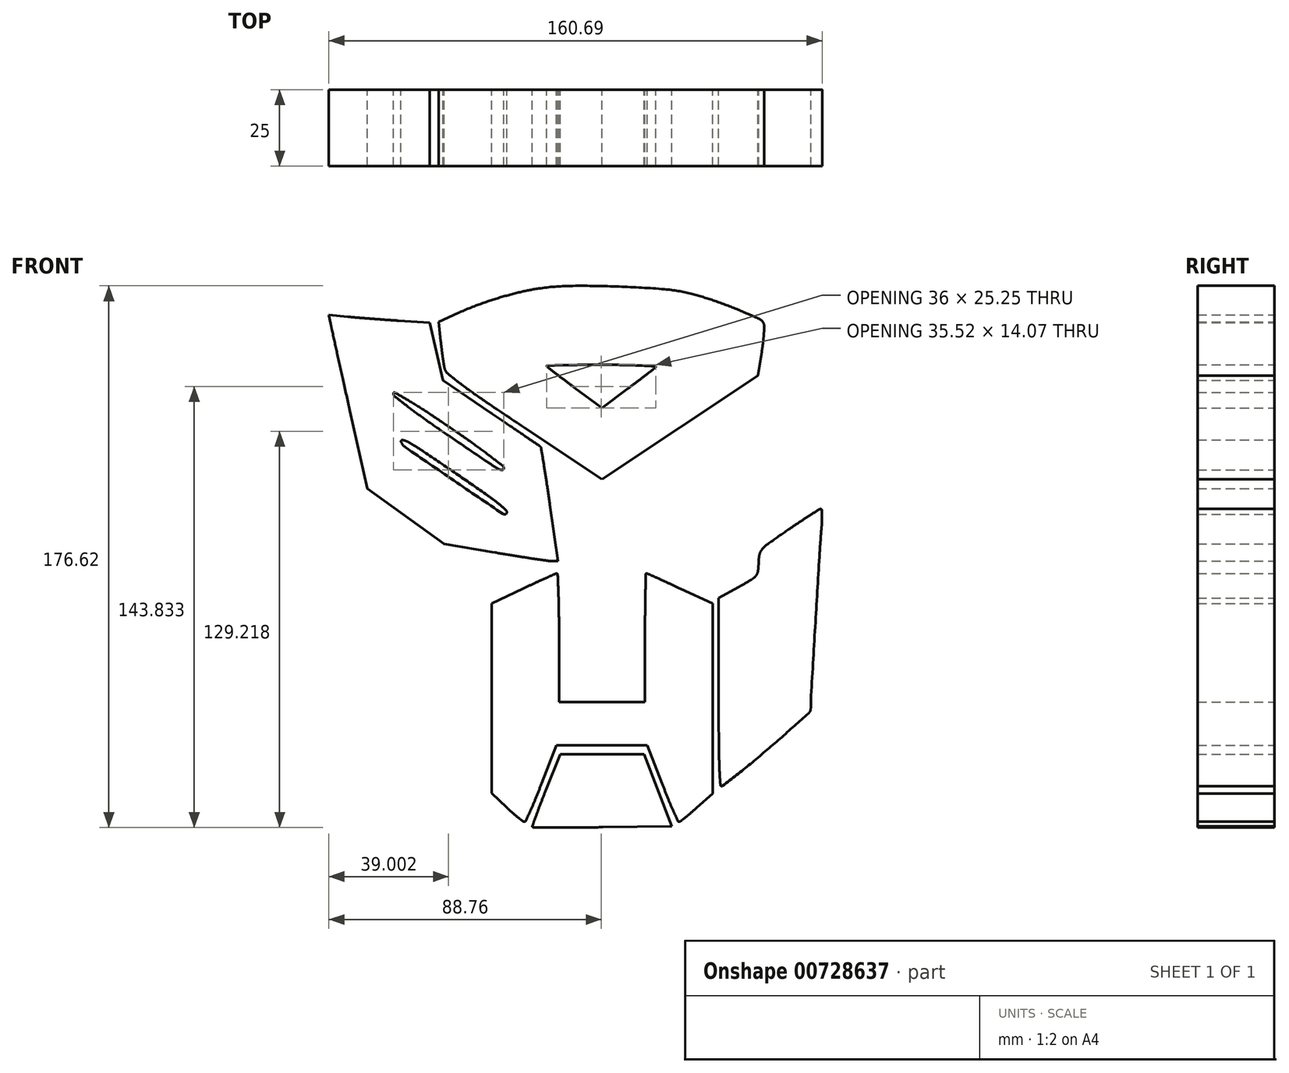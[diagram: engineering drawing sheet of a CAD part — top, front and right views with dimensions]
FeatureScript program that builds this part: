
annotation { "Feature Type Name" : "Feature", "Feature Type Description" : "" }
export const myFeature = defineFeature(function(context is Context, id is Id, definition is map)
    precondition{}
    {
        {
            var Q0;
            Q0=qCreatedBy(makeId("Front.planeOp"),FACE);
            var sketch = newSketch(context, id + "F0", { "sketchPlane" : qUnion([Q0])});
            skArc(sketch, "E0", {"start": v(-19.83, 87.54) * mm, "mid": v(-23, 87.02) * mm, "end": v(-26.16, 86.36) * mm});
            skArc(sketch, "E1", {"start": v(-26.16, 86.36) * mm, "mid": v(-29.68, 85.48) * mm, "end": v(-33.17, 84.5) * mm});
            skArc(sketch, "E2", {"start": v(-33.17, 84.5) * mm, "mid": v(-36.72, 83.37) * mm, "end": v(-40.23, 82.14) * mm});
            skArc(sketch, "E3", {"start": v(-40.23, 82.14) * mm, "mid": v(-43.53, 80.85) * mm, "end": v(-46.77, 79.46) * mm});
            skLineSegment(sketch, "E4", {"start": v(-46.77, 79.46) * mm, "end": v(-53.15, 76.56) * mm});
            skLineSegment(sketch, "E5", {"start": v(-53.15, 76.56) * mm, "end": v(-52.44, 70.3) * mm});
            skArc(sketch, "E6", {"start": v(-52.44, 70.3) * mm, "mid": v(-52.3, 69.02) * mm, "end": v(-52.13, 67.73) * mm});
            skArc(sketch, "E7", {"start": v(-52.13, 67.73) * mm, "mid": v(-51.97, 66.44) * mm, "end": v(-51.8, 65.16) * mm});
            skArc(sketch, "E8", {"start": v(-51.8, 65.16) * mm, "mid": v(-51.63, 64.04) * mm, "end": v(-51.47, 62.92) * mm});
            skArc(sketch, "E9", {"start": v(-51.47, 62.92) * mm, "mid": v(-51.36, 62.23) * mm, "end": v(-51.23, 61.56) * mm});
            skArc(sketch, "E10", {"start": v(-51.23, 61.56) * mm, "mid": v(-50.83, 60.52) * mm, "end": v(-50.11, 59.68) * mm});
            skArc(sketch, "E11", {"start": v(-50.11, 59.68) * mm, "mid": v(-47.88, 57.85) * mm, "end": v(-45.6, 56.09) * mm});
            skArc(sketch, "E12", {"start": v(-45.6, 56.09) * mm, "mid": v(-41.96, 53.43) * mm, "end": v(-38.27, 50.86) * mm});
            skArc(sketch, "E13", {"start": v(-38.27, 50.86) * mm, "mid": v(-31.8, 46.5) * mm, "end": v(-25.3, 42.15) * mm});
            skLineSegment(sketch, "E14", {"start": v(-25.3, 42.15) * mm, "end": v(0.11, 25.25) * mm});
            skLineSegment(sketch, "E15", {"start": v(0.11, 25.25) * mm, "end": v(25.52, 42.15) * mm});
            skLineSegment(sketch, "E16", {"start": v(25.52, 42.15) * mm, "end": v(50.94, 59.06) * mm});
            skLineSegment(sketch, "E17", {"start": v(50.94, 59.06) * mm, "end": v(52.14, 66.78) * mm});
            skArc(sketch, "E18", {"start": v(52.14, 66.78) * mm, "mid": v(52.37, 68.3) * mm, "end": v(52.56, 69.84) * mm});
            skArc(sketch, "E19", {"start": v(52.56, 69.84) * mm, "mid": v(52.72, 71.24) * mm, "end": v(52.84, 72.64) * mm});
            skArc(sketch, "E20", {"start": v(52.84, 72.64) * mm, "mid": v(52.91, 73.81) * mm, "end": v(52.96, 74.98) * mm});
            skArc(sketch, "E21", {"start": v(52.96, 74.98) * mm, "mid": v(52.93, 75.45) * mm, "end": v(52.81, 75.9) * mm});
            skArc(sketch, "E22", {"start": v(52.81, 75.9) * mm, "mid": v(52.21, 76.85) * mm, "end": v(51.3, 77.5) * mm});
            skArc(sketch, "E23", {"start": v(51.3, 77.5) * mm, "mid": v(47.91, 79.04) * mm, "end": v(44.5, 80.5) * mm});
            skArc(sketch, "E24", {"start": v(44.5, 80.5) * mm, "mid": v(40.67, 82.02) * mm, "end": v(36.8, 83.42) * mm});
            skArc(sketch, "E25", {"start": v(36.8, 83.42) * mm, "mid": v(33.06, 84.63) * mm, "end": v(29.29, 85.7) * mm});
            skArc(sketch, "E26", {"start": v(29.29, 85.7) * mm, "mid": v(24.9, 86.64) * mm, "end": v(20.46, 87.2) * mm});
            skArc(sketch, "E27", {"start": v(20.46, 87.2) * mm, "mid": v(13.05, 87.72) * mm, "end": v(5.63, 88.07) * mm});
            skArc(sketch, "E28", {"start": v(5.63, 88.07) * mm, "mid": v(-1.91, 88.27) * mm, "end": v(-9.45, 88.3) * mm});
            skArc(sketch, "E29", {"start": v(-9.45, 88.3) * mm, "mid": v(-14.65, 88.09) * mm, "end": v(-19.83, 87.54) * mm});
            skArc(sketch, "E30", {"start": v(17.56, 61.7) * mm, "mid": v(17.23, 61.42) * mm, "end": v(16.88, 61.15) * mm});
            skArc(sketch, "E31", {"start": v(16.88, 61.15) * mm, "mid": v(15.68, 60.22) * mm, "end": v(14.47, 59.3) * mm});
            skArc(sketch, "E32", {"start": v(14.47, 59.3) * mm, "mid": v(13.04, 58.2) * mm, "end": v(11.6, 57.1) * mm});
            skArc(sketch, "E33", {"start": v(11.6, 57.1) * mm, "mid": v(10, 55.9) * mm, "end": v(8.38, 54.68) * mm});
            skLineSegment(sketch, "E34", {"start": v(8.38, 54.68) * mm, "end": v(0.14, 48.5) * mm});
            skLineSegment(sketch, "E35", {"start": v(0.14, 48.5) * mm, "end": v(-8.87, 55.15) * mm});
            skArc(sketch, "E36", {"start": v(-8.87, 55.15) * mm, "mid": v(-10.6, 56.44) * mm, "end": v(-12.33, 57.73) * mm});
            skArc(sketch, "E37", {"start": v(-12.33, 57.73) * mm, "mid": v(-13.79, 58.84) * mm, "end": v(-15.24, 59.97) * mm});
            skArc(sketch, "E38", {"start": v(-15.24, 59.97) * mm, "mid": v(-16.5, 60.96) * mm, "end": v(-17.77, 61.95) * mm});
            skArc(sketch, "E39", {"start": v(-17.77, 61.95) * mm, "mid": v(-17.86, 62.05) * mm, "end": v(-17.89, 62.19) * mm});
            skArc(sketch, "E40", {"start": v(-17.89, 62.19) * mm, "mid": v(-17.84, 62.3) * mm, "end": v(-17.74, 62.34) * mm});
            skArc(sketch, "E41", {"start": v(-17.74, 62.34) * mm, "mid": v(-15.14, 62.4) * mm, "end": v(-12.54, 62.45) * mm});
            skArc(sketch, "E42", {"start": v(-12.54, 62.45) * mm, "mid": v(-9.6, 62.5) * mm, "end": v(-6.67, 62.53) * mm});
            skArc(sketch, "E43", {"start": v(-6.67, 62.53) * mm, "mid": v(-3.18, 62.55) * mm, "end": v(0.31, 62.56) * mm});
            skArc(sketch, "E44", {"start": v(0.31, 62.56) * mm, "mid": v(3.77, 62.54) * mm, "end": v(7.23, 62.5) * mm});
            skArc(sketch, "E45", {"start": v(7.23, 62.5) * mm, "mid": v(10.06, 62.42) * mm, "end": v(12.89, 62.3) * mm});
            skArc(sketch, "E46", {"start": v(12.89, 62.3) * mm, "mid": v(15.17, 62.19) * mm, "end": v(17.45, 62.05) * mm});
            skArc(sketch, "E47", {"start": v(17.45, 62.05) * mm, "mid": v(17.62, 61.92) * mm, "end": v(17.56, 61.7) * mm});
            skArc(sketch, "E48", {"start": v(-88.3, 75.94) * mm, "mid": v(-88.08, 74.93) * mm, "end": v(-87.87, 73.92) * mm});
            skArc(sketch, "E49", {"start": v(-87.87, 73.92) * mm, "mid": v(-87.04, 70.17) * mm, "end": v(-86.21, 66.43) * mm});
            skArc(sketch, "E50", {"start": v(-86.21, 66.43) * mm, "mid": v(-85.24, 62) * mm, "end": v(-84.25, 57.57) * mm});
            skArc(sketch, "E51", {"start": v(-84.25, 57.57) * mm, "mid": v(-83.15, 52.59) * mm, "end": v(-82.04, 47.61) * mm});
            skLineSegment(sketch, "E52", {"start": v(-82.04, 47.61) * mm, "end": v(-76.39, 22.17) * mm});
            skLineSegment(sketch, "E53", {"start": v(-76.39, 22.17) * mm, "end": v(-63.89, 13.17) * mm});
            skLineSegment(sketch, "E54", {"start": v(-63.89, 13.17) * mm, "end": v(-51.39, 4.18) * mm});
            skLineSegment(sketch, "E55", {"start": v(-51.39, 4.18) * mm, "end": v(-34.89, 1.38) * mm});
            skArc(sketch, "E56", {"start": v(-34.89, 1.38) * mm, "mid": v(-31.65, 0.84) * mm, "end": v(-28.42, 0.3) * mm});
            skArc(sketch, "E57", {"start": v(-28.42, 0.3) * mm, "mid": v(-25.52, -0.15) * mm, "end": v(-22.63, -0.6) * mm});
            skArc(sketch, "E58", {"start": v(-22.63, -0.6) * mm, "mid": v(-20.18, -0.97) * mm, "end": v(-17.74, -1.32) * mm});
            skArc(sketch, "E59", {"start": v(-17.74, -1.32) * mm, "mid": v(-17.03, -1.4) * mm, "end": v(-16.31, -1.43) * mm});
            skLineSegment(sketch, "E60", {"start": v(-16.31, -1.43) * mm, "end": v(-14.24, -1.44) * mm});
            skLineSegment(sketch, "E61", {"start": v(-14.24, -1.44) * mm, "end": v(-16.89, 17.04) * mm});
            skArc(sketch, "E62", {"start": v(-16.89, 17.04) * mm, "mid": v(-17.4, 20.6) * mm, "end": v(-17.93, 24.16) * mm});
            skArc(sketch, "E63", {"start": v(-17.93, 24.16) * mm, "mid": v(-18.4, 27.18) * mm, "end": v(-18.88, 30.2) * mm});
            skArc(sketch, "E64", {"start": v(-18.88, 30.2) * mm, "mid": v(-19.32, 32.86) * mm, "end": v(-19.76, 35.53) * mm});
            skArc(sketch, "E65", {"start": v(-19.76, 35.53) * mm, "mid": v(-19.83, 35.72) * mm, "end": v(-19.96, 35.87) * mm});
            skArc(sketch, "E66", {"start": v(-19.96, 35.87) * mm, "mid": v(-20.13, 36) * mm, "end": v(-20.3, 36.13) * mm});
            skArc(sketch, "E67", {"start": v(-20.3, 36.13) * mm, "mid": v(-22.59, 37.69) * mm, "end": v(-24.86, 39.25) * mm});
            skArc(sketch, "E68", {"start": v(-24.86, 39.25) * mm, "mid": v(-27.44, 41) * mm, "end": v(-30.02, 42.76) * mm});
            skArc(sketch, "E69", {"start": v(-30.02, 42.76) * mm, "mid": v(-33.03, 44.82) * mm, "end": v(-36.05, 46.87) * mm});
            skLineSegment(sketch, "E70", {"start": v(-36.05, 46.87) * mm, "end": v(-51.72, 57.53) * mm});
            skLineSegment(sketch, "E71", {"start": v(-51.72, 57.53) * mm, "end": v(-53.85, 66.9) * mm});
            skLineSegment(sketch, "E72", {"start": v(-53.85, 66.9) * mm, "end": v(-55.99, 76.28) * mm});
            skLineSegment(sketch, "E73", {"start": v(-55.99, 76.28) * mm, "end": v(-66.19, 76.95) * mm});
            skArc(sketch, "E74", {"start": v(-66.19, 76.95) * mm, "mid": v(-68.37, 77.1) * mm, "end": v(-70.55, 77.25) * mm});
            skArc(sketch, "E75", {"start": v(-70.55, 77.25) * mm, "mid": v(-72.89, 77.42) * mm, "end": v(-75.23, 77.6) * mm});
            skArc(sketch, "E76", {"start": v(-75.23, 77.6) * mm, "mid": v(-77.38, 77.77) * mm, "end": v(-79.54, 77.94) * mm});
            skArc(sketch, "E77", {"start": v(-79.54, 77.94) * mm, "mid": v(-81.09, 78.08) * mm, "end": v(-82.64, 78.22) * mm});
            skLineSegment(sketch, "E78", {"start": v(-82.64, 78.22) * mm, "end": v(-88.9, 78.83) * mm});
            skLineSegment(sketch, "E79", {"start": v(-88.9, 78.83) * mm, "end": v(-88.3, 75.94) * mm});
            skArc(sketch, "E80", {"start": v(-31.89, 28.83) * mm, "mid": v(-32.06, 28.43) * mm, "end": v(-32.47, 28.29) * mm});
            skArc(sketch, "E81", {"start": v(-32.47, 28.29) * mm, "mid": v(-33.17, 28.42) * mm, "end": v(-33.83, 28.71) * mm});
            skArc(sketch, "E82", {"start": v(-33.83, 28.71) * mm, "mid": v(-35.5, 29.75) * mm, "end": v(-37.15, 30.83) * mm});
            skArc(sketch, "E83", {"start": v(-37.15, 30.83) * mm, "mid": v(-44.15, 35.57) * mm, "end": v(-51.14, 40.31) * mm});
            skArc(sketch, "E84", {"start": v(-51.14, 40.31) * mm, "mid": v(-54.36, 42.53) * mm, "end": v(-57.56, 44.78) * mm});
            skArc(sketch, "E85", {"start": v(-57.56, 44.78) * mm, "mid": v(-60.28, 46.76) * mm, "end": v(-62.97, 48.79) * mm});
            skArc(sketch, "E86", {"start": v(-62.97, 48.79) * mm, "mid": v(-65.22, 50.53) * mm, "end": v(-67.46, 52.3) * mm});
            skArc(sketch, "E87", {"start": v(-67.46, 52.3) * mm, "mid": v(-67.77, 52.69) * mm, "end": v(-67.89, 53.18) * mm});
            skArc(sketch, "E88", {"start": v(-67.89, 53.18) * mm, "mid": v(-67.71, 53.48) * mm, "end": v(-67.37, 53.49) * mm});
            skArc(sketch, "E89", {"start": v(-67.37, 53.49) * mm, "mid": v(-65.2, 52.25) * mm, "end": v(-63.06, 51) * mm});
            skArc(sketch, "E90", {"start": v(-63.06, 51) * mm, "mid": v(-60.22, 49.26) * mm, "end": v(-57.4, 47.46) * mm});
            skArc(sketch, "E91", {"start": v(-57.4, 47.46) * mm, "mid": v(-53.64, 44.97) * mm, "end": v(-49.89, 42.45) * mm});
            skArc(sketch, "E92", {"start": v(-49.89, 42.45) * mm, "mid": v(-46.43, 40.07) * mm, "end": v(-42.99, 37.66) * mm});
            skArc(sketch, "E93", {"start": v(-42.99, 37.66) * mm, "mid": v(-40.06, 35.55) * mm, "end": v(-37.18, 33.4) * mm});
            skArc(sketch, "E94", {"start": v(-37.18, 33.4) * mm, "mid": v(-34.73, 31.54) * mm, "end": v(-32.3, 29.67) * mm});
            skArc(sketch, "E95", {"start": v(-32.3, 29.67) * mm, "mid": v(-32, 29.3) * mm, "end": v(-31.89, 28.83) * mm});
            skArc(sketch, "E96", {"start": v(-47.37, 27.03) * mm, "mid": v(-42.58, 23.74) * mm, "end": v(-37.8, 20.42) * mm});
            skArc(sketch, "E97", {"start": v(-37.8, 20.42) * mm, "mid": v(-35.56, 18.8) * mm, "end": v(-33.36, 17.1) * mm});
            skArc(sketch, "E98", {"start": v(-33.36, 17.1) * mm, "mid": v(-32.2, 16.1) * mm, "end": v(-31.1, 15.03) * mm});
            skArc(sketch, "E99", {"start": v(-31.1, 15.03) * mm, "mid": v(-30.9, 14.51) * mm, "end": v(-31.11, 14) * mm});
            skArc(sketch, "E100", {"start": v(-31.11, 14) * mm, "mid": v(-31.6, 13.76) * mm, "end": v(-32.14, 13.9) * mm});
            skArc(sketch, "E101", {"start": v(-32.14, 13.9) * mm, "mid": v(-40.2, 19.39) * mm, "end": v(-48.24, 24.88) * mm});
            skArc(sketch, "E102", {"start": v(-48.24, 24.88) * mm, "mid": v(-56.1, 30.27) * mm, "end": v(-63.95, 35.68) * mm});
            skArc(sketch, "E103", {"start": v(-63.95, 35.68) * mm, "mid": v(-64.78, 36.44) * mm, "end": v(-65.35, 37.42) * mm});
            skArc(sketch, "E104", {"start": v(-65.35, 37.42) * mm, "mid": v(-65.28, 37.87) * mm, "end": v(-64.84, 38.03) * mm});
            skArc(sketch, "E105", {"start": v(-64.84, 38.03) * mm, "mid": v(-63.8, 37.72) * mm, "end": v(-62.8, 37.25) * mm});
            skArc(sketch, "E106", {"start": v(-62.8, 37.25) * mm, "mid": v(-60.4, 35.8) * mm, "end": v(-58.03, 34.26) * mm});
            skArc(sketch, "E107", {"start": v(-58.03, 34.26) * mm, "mid": v(-52.7, 30.66) * mm, "end": v(-47.37, 27.03) * mm});
            skArc(sketch, "E108", {"start": v(80.61, 78.05) * mm, "mid": v(80.25, 77.94) * mm, "end": v(79.87, 77.89) * mm});
            skArc(sketch, "E109", {"start": v(79.87, 77.89) * mm, "mid": v(78.17, 77.74) * mm, "end": v(76.47, 77.6) * mm});
            skArc(sketch, "E110", {"start": v(76.47, 77.6) * mm, "mid": v(74.47, 77.45) * mm, "end": v(72.47, 77.31) * mm});
            skArc(sketch, "E111", {"start": v(72.47, 77.31) * mm, "mid": v(70.2, 77.17) * mm, "end": v(67.91, 77.03) * mm});
            skLineSegment(sketch, "E112", {"start": v(67.91, 77.03) * mm, "end": v(56.21, 76.36) * mm});
            skLineSegment(sketch, "E113", {"start": v(56.21, 76.36) * mm, "end": v(54.05, 67) * mm});
            skLineSegment(sketch, "E114", {"start": v(54.05, 67) * mm, "end": v(51.89, 57.65) * mm});
            skLineSegment(sketch, "E115", {"start": v(51.89, 57.65) * mm, "end": v(36.25, 46.94) * mm});
            skArc(sketch, "E116", {"start": v(36.25, 46.94) * mm, "mid": v(33.24, 44.88) * mm, "end": v(30.23, 42.81) * mm});
            skArc(sketch, "E117", {"start": v(30.23, 42.81) * mm, "mid": v(27.66, 41.05) * mm, "end": v(25.09, 39.28) * mm});
            skArc(sketch, "E118", {"start": v(25.09, 39.28) * mm, "mid": v(22.81, 37.72) * mm, "end": v(20.54, 36.15) * mm});
            skArc(sketch, "E119", {"start": v(20.54, 36.15) * mm, "mid": v(20.37, 36.03) * mm, "end": v(20.2, 35.9) * mm});
            skArc(sketch, "E120", {"start": v(20.2, 35.9) * mm, "mid": v(19.86, 35.5) * mm, "end": v(19.7, 35) * mm});
            skArc(sketch, "E121", {"start": v(19.7, 35) * mm, "mid": v(18.38, 26.14) * mm, "end": v(17.07, 17.28) * mm});
            skArc(sketch, "E122", {"start": v(17.07, 17.28) * mm, "mid": v(15.76, 8.38) * mm, "end": v(14.45, -0.52) * mm});
            skArc(sketch, "E123", {"start": v(14.45, -0.52) * mm, "mid": v(14.49, -0.97) * mm, "end": v(14.71, -1.35) * mm});
            skArc(sketch, "E124", {"start": v(14.71, -1.35) * mm, "mid": v(14.88, -1.46) * mm, "end": v(15.08, -1.48) * mm});
            skArc(sketch, "E125", {"start": v(15.08, -1.48) * mm, "mid": v(17.68, -1.14) * mm, "end": v(20.29, -0.8) * mm});
            skArc(sketch, "E126", {"start": v(20.29, -0.8) * mm, "mid": v(23.25, -0.4) * mm, "end": v(26.2, 0.03) * mm});
            skArc(sketch, "E127", {"start": v(26.2, 0.03) * mm, "mid": v(29.68, 0.55) * mm, "end": v(33.16, 1.1) * mm});
            skLineSegment(sketch, "E128", {"start": v(33.16, 1.1) * mm, "end": v(51.22, 3.94) * mm});
            skLineSegment(sketch, "E129", {"start": v(51.22, 3.94) * mm, "end": v(63.94, 13.16) * mm});
            skLineSegment(sketch, "E130", {"start": v(63.94, 13.16) * mm, "end": v(76.66, 22.37) * mm});
            skLineSegment(sketch, "E131", {"start": v(76.66, 22.37) * mm, "end": v(82.52, 49.22) * mm});
            skArc(sketch, "E132", {"start": v(82.52, 49.22) * mm, "mid": v(83.66, 54.4) * mm, "end": v(84.8, 59.6) * mm});
            skArc(sketch, "E133", {"start": v(84.8, 59.6) * mm, "mid": v(85.8, 64.07) * mm, "end": v(86.8, 68.54) * mm});
            skArc(sketch, "E134", {"start": v(86.8, 68.54) * mm, "mid": v(87.68, 72.43) * mm, "end": v(88.56, 76.32) * mm});
            skArc(sketch, "E135", {"start": v(88.56, 76.32) * mm, "mid": v(88.69, 76.82) * mm, "end": v(88.85, 77.3) * mm});
            skArc(sketch, "E136", {"start": v(88.85, 77.3) * mm, "mid": v(88.89, 77.59) * mm, "end": v(88.8, 77.85) * mm});
            skArc(sketch, "E137", {"start": v(88.8, 77.85) * mm, "mid": v(88.58, 78.09) * mm, "end": v(88.3, 78.24) * mm});
            skArc(sketch, "E138", {"start": v(88.3, 78.24) * mm, "mid": v(87.77, 78.38) * mm, "end": v(87.23, 78.45) * mm});
            skArc(sketch, "E139", {"start": v(87.23, 78.45) * mm, "mid": v(86.35, 78.48) * mm, "end": v(85.47, 78.48) * mm});
            skArc(sketch, "E140", {"start": v(85.47, 78.48) * mm, "mid": v(84.7, 78.45) * mm, "end": v(83.92, 78.42) * mm});
            skArc(sketch, "E141", {"start": v(83.92, 78.42) * mm, "mid": v(83.19, 78.38) * mm, "end": v(82.45, 78.32) * mm});
            skArc(sketch, "E142", {"start": v(82.45, 78.32) * mm, "mid": v(81.83, 78.26) * mm, "end": v(81.22, 78.19) * mm});
            skArc(sketch, "E143", {"start": v(81.22, 78.19) * mm, "mid": v(80.91, 78.13) * mm, "end": v(80.61, 78.05) * mm});
            skArc(sketch, "E144", {"start": v(68.11, 53.07) * mm, "mid": v(67.94, 52.34) * mm, "end": v(67.45, 51.76) * mm});
            skArc(sketch, "E145", {"start": v(67.45, 51.76) * mm, "mid": v(63.76, 49.05) * mm, "end": v(60.05, 46.37) * mm});
            skArc(sketch, "E146", {"start": v(60.05, 46.37) * mm, "mid": v(55.02, 42.8) * mm, "end": v(49.95, 39.32) * mm});
            skArc(sketch, "E147", {"start": v(49.95, 39.32) * mm, "mid": v(42.43, 34.25) * mm, "end": v(34.9, 29.2) * mm});
            skArc(sketch, "E148", {"start": v(34.9, 29.2) * mm, "mid": v(34.12, 28.7) * mm, "end": v(33.33, 28.22) * mm});
            skArc(sketch, "E149", {"start": v(33.33, 28.22) * mm, "mid": v(32.99, 28.06) * mm, "end": v(32.62, 27.97) * mm});
            skArc(sketch, "E150", {"start": v(32.62, 27.97) * mm, "mid": v(32.4, 28.02) * mm, "end": v(32.25, 28.2) * mm});
            skArc(sketch, "E151", {"start": v(32.25, 28.2) * mm, "mid": v(32.15, 28.54) * mm, "end": v(32.11, 28.9) * mm});
            skArc(sketch, "E152", {"start": v(32.11, 28.9) * mm, "mid": v(32.23, 29.42) * mm, "end": v(32.57, 29.84) * mm});
            skArc(sketch, "E153", {"start": v(32.57, 29.84) * mm, "mid": v(34.88, 31.65) * mm, "end": v(37.2, 33.44) * mm});
            skArc(sketch, "E154", {"start": v(37.2, 33.44) * mm, "mid": v(40.04, 35.56) * mm, "end": v(42.9, 37.62) * mm});
            skArc(sketch, "E155", {"start": v(42.9, 37.62) * mm, "mid": v(46.37, 40.05) * mm, "end": v(49.86, 42.44) * mm});
            skArc(sketch, "E156", {"start": v(49.86, 42.44) * mm, "mid": v(53.27, 44.74) * mm, "end": v(56.69, 47.05) * mm});
            skArc(sketch, "E157", {"start": v(56.69, 47.05) * mm, "mid": v(59.58, 49) * mm, "end": v(62.47, 50.94) * mm});
            skArc(sketch, "E158", {"start": v(62.47, 50.94) * mm, "mid": v(65.07, 52.68) * mm, "end": v(67.67, 54.42) * mm});
            skArc(sketch, "E159", {"start": v(67.67, 54.42) * mm, "mid": v(67.76, 54.47) * mm, "end": v(67.86, 54.5) * mm});
            skArc(sketch, "E160", {"start": v(67.86, 54.5) * mm, "mid": v(67.92, 54.5) * mm, "end": v(67.96, 54.44) * mm});
            skArc(sketch, "E161", {"start": v(67.96, 54.44) * mm, "mid": v(68, 54.27) * mm, "end": v(68.04, 54.1) * mm});
            skArc(sketch, "E162", {"start": v(68.04, 54.1) * mm, "mid": v(68.07, 53.87) * mm, "end": v(68.1, 53.64) * mm});
            skArc(sketch, "E163", {"start": v(68.1, 53.64) * mm, "mid": v(68.1, 53.35) * mm, "end": v(68.11, 53.07) * mm});
            skArc(sketch, "E164", {"start": v(65.52, 37.3) * mm, "mid": v(64.78, 36.07) * mm, "end": v(63.72, 35.1) * mm});
            skArc(sketch, "E165", {"start": v(63.72, 35.1) * mm, "mid": v(55.98, 29.92) * mm, "end": v(48.22, 24.77) * mm});
            skArc(sketch, "E166", {"start": v(48.22, 24.77) * mm, "mid": v(40.26, 19.5) * mm, "end": v(32.28, 14.26) * mm});
            skArc(sketch, "E167", {"start": v(32.28, 14.26) * mm, "mid": v(31.68, 14.19) * mm, "end": v(31.26, 14.61) * mm});
            skArc(sketch, "E168", {"start": v(31.26, 14.61) * mm, "mid": v(31.2, 14.83) * mm, "end": v(31.15, 15.04) * mm});
            skArc(sketch, "E169", {"start": v(31.15, 15.04) * mm, "mid": v(31.12, 15.25) * mm, "end": v(31.11, 15.45) * mm});
            skArc(sketch, "E170", {"start": v(31.11, 15.45) * mm, "mid": v(31.12, 15.62) * mm, "end": v(31.15, 15.8) * mm});
            skArc(sketch, "E171", {"start": v(31.15, 15.8) * mm, "mid": v(31.19, 15.9) * mm, "end": v(31.26, 15.98) * mm});
            skArc(sketch, "E172", {"start": v(31.26, 15.98) * mm, "mid": v(32.78, 17.19) * mm, "end": v(34.36, 18.3) * mm});
            skArc(sketch, "E173", {"start": v(34.36, 18.3) * mm, "mid": v(41.62, 23.15) * mm, "end": v(48.87, 27.98) * mm});
            skArc(sketch, "E174", {"start": v(48.87, 27.98) * mm, "mid": v(56.66, 33.15) * mm, "end": v(64.44, 38.31) * mm});
            skArc(sketch, "E175", {"start": v(64.44, 38.31) * mm, "mid": v(64.83, 38.5) * mm, "end": v(65.24, 38.56) * mm});
            skArc(sketch, "E176", {"start": v(65.24, 38.56) * mm, "mid": v(65.38, 38.53) * mm, "end": v(65.5, 38.45) * mm});
            skArc(sketch, "E177", {"start": v(65.5, 38.45) * mm, "mid": v(65.6, 38.33) * mm, "end": v(65.66, 38.19) * mm});
            skArc(sketch, "E178", {"start": v(65.66, 38.19) * mm, "mid": v(65.68, 37.99) * mm, "end": v(65.67, 37.78) * mm});
            skArc(sketch, "E179", {"start": v(65.67, 37.78) * mm, "mid": v(65.6, 37.54) * mm, "end": v(65.52, 37.3) * mm});
            skArc(sketch, "E180", {"start": v(-17.43, 31.36) * mm, "mid": v(-17.26, 30.58) * mm, "end": v(-17.12, 29.8) * mm});
            skArc(sketch, "E181", {"start": v(-17.12, 29.8) * mm, "mid": v(-16.72, 27.4) * mm, "end": v(-16.32, 25) * mm});
            skArc(sketch, "E182", {"start": v(-16.32, 25) * mm, "mid": v(-15.85, 22.13) * mm, "end": v(-15.4, 19.27) * mm});
            skArc(sketch, "E183", {"start": v(-15.4, 19.27) * mm, "mid": v(-14.9, 16.1) * mm, "end": v(-14.4, 12.93) * mm});
            skArc(sketch, "E184", {"start": v(-14.4, 12.93) * mm, "mid": v(-13.7, 8.27) * mm, "end": v(-13.1, 3.6) * mm});
            skArc(sketch, "E185", {"start": v(-13.1, 3.6) * mm, "mid": v(-12.67, -0.27) * mm, "end": v(-12.36, -4.14) * mm});
            skArc(sketch, "E186", {"start": v(-12.36, -4.14) * mm, "mid": v(-12.13, -8.35) * mm, "end": v(-12, -12.57) * mm});
            skArc(sketch, "E187", {"start": v(-12, -12.57) * mm, "mid": v(-11.91, -18.45) * mm, "end": v(-11.89, -24.32) * mm});
            skLineSegment(sketch, "E188", {"start": v(-11.89, -24.32) * mm, "end": v(-11.89, -45.44) * mm});
            skLineSegment(sketch, "E189", {"start": v(-11.89, -45.44) * mm, "end": v(0.11, -45.44) * mm});
            skLineSegment(sketch, "E190", {"start": v(0.11, -45.44) * mm, "end": v(12.11, -45.44) * mm});
            skLineSegment(sketch, "E191", {"start": v(12.11, -45.44) * mm, "end": v(12.11, -23.9) * mm});
            skArc(sketch, "E192", {"start": v(12.11, -23.9) * mm, "mid": v(12.14, -17.85) * mm, "end": v(12.22, -11.8) * mm});
            skArc(sketch, "E193", {"start": v(12.22, -11.8) * mm, "mid": v(12.34, -7.63) * mm, "end": v(12.57, -3.45) * mm});
            skArc(sketch, "E194", {"start": v(12.57, -3.45) * mm, "mid": v(12.88, 0.32) * mm, "end": v(13.3, 4.08) * mm});
            skArc(sketch, "E195", {"start": v(13.3, 4.08) * mm, "mid": v(13.92, 8.62) * mm, "end": v(14.61, 13.15) * mm});
            skArc(sketch, "E196", {"start": v(14.61, 13.15) * mm, "mid": v(15.87, 21.03) * mm, "end": v(17.1, 28.91) * mm});
            skArc(sketch, "E197", {"start": v(17.1, 28.91) * mm, "mid": v(17.12, 30.26) * mm, "end": v(16.78, 31.56) * mm});
            skArc(sketch, "E198", {"start": v(16.78, 31.56) * mm, "mid": v(16.13, 32.17) * mm, "end": v(15.24, 32.08) * mm});
            skArc(sketch, "E199", {"start": v(15.24, 32.08) * mm, "mid": v(11.9, 30.04) * mm, "end": v(8.61, 27.91) * mm});
            skLineSegment(sketch, "E200", {"start": v(8.61, 27.91) * mm, "end": v(0.12, 22.26) * mm});
            skLineSegment(sketch, "E201", {"start": v(0.12, 22.26) * mm, "end": v(-6.64, 26.74) * mm});
            skArc(sketch, "E202", {"start": v(-6.64, 26.74) * mm, "mid": v(-8, 27.65) * mm, "end": v(-9.39, 28.55) * mm});
            skArc(sketch, "E203", {"start": v(-9.39, 28.55) * mm, "mid": v(-10.73, 29.41) * mm, "end": v(-12.07, 30.27) * mm});
            skArc(sketch, "E204", {"start": v(-12.07, 30.27) * mm, "mid": v(-13.23, 31) * mm, "end": v(-14.39, 31.7) * mm});
            skArc(sketch, "E205", {"start": v(-14.39, 31.7) * mm, "mid": v(-15.02, 32.09) * mm, "end": v(-15.67, 32.44) * mm});
            skArc(sketch, "E206", {"start": v(-15.67, 32.44) * mm, "mid": v(-16.36, 32.8) * mm, "end": v(-17.07, 33.14) * mm});
            skArc(sketch, "E207", {"start": v(-17.07, 33.14) * mm, "mid": v(-17.3, 33.19) * mm, "end": v(-17.52, 33.12) * mm});
            skArc(sketch, "E208", {"start": v(-17.52, 33.12) * mm, "mid": v(-17.67, 32.95) * mm, "end": v(-17.7, 32.74) * mm});
            skArc(sketch, "E209", {"start": v(-17.7, 32.74) * mm, "mid": v(-17.57, 32.04) * mm, "end": v(-17.43, 31.36) * mm});
            skArc(sketch, "E210", {"start": v(-71.4, 8.3) * mm, "mid": v(-71.11, 4.35) * mm, "end": v(-70.86, 0.38) * mm});
            skArc(sketch, "E211", {"start": v(-70.86, 0.38) * mm, "mid": v(-70.15, -11.2) * mm, "end": v(-69.46, -22.8) * mm});
            skArc(sketch, "E212", {"start": v(-69.46, -22.8) * mm, "mid": v(-68.71, -35.24) * mm, "end": v(-67.97, -47.69) * mm});
            skArc(sketch, "E213", {"start": v(-67.97, -47.69) * mm, "mid": v(-67.9, -49.08) * mm, "end": v(-67.89, -50.48) * mm});
            skArc(sketch, "E214", {"start": v(-67.89, -50.48) * mm, "mid": v(-67.78, -50.95) * mm, "end": v(-67.49, -51.34) * mm});
            skArc(sketch, "E215", {"start": v(-67.49, -51.34) * mm, "mid": v(-61.08, -56.77) * mm, "end": v(-54.68, -62.2) * mm});
            skArc(sketch, "E216", {"start": v(-54.68, -62.2) * mm, "mid": v(-48.77, -67.18) * mm, "end": v(-42.84, -72.14) * mm});
            skArc(sketch, "E217", {"start": v(-42.84, -72.14) * mm, "mid": v(-41.04, -73.54) * mm, "end": v(-39.14, -74.8) * mm});
            skArc(sketch, "E218", {"start": v(-39.14, -74.8) * mm, "mid": v(-38.7, -74.81) * mm, "end": v(-38.45, -74.45) * mm});
            skArc(sketch, "E219", {"start": v(-38.45, -74.45) * mm, "mid": v(-38.28, -71.78) * mm, "end": v(-38.14, -69.12) * mm});
            skArc(sketch, "E220", {"start": v(-38.14, -69.12) * mm, "mid": v(-38, -64.84) * mm, "end": v(-37.94, -60.56) * mm});
            skArc(sketch, "E221", {"start": v(-37.94, -60.56) * mm, "mid": v(-37.9, -52.58) * mm, "end": v(-37.89, -44.59) * mm});
            skLineSegment(sketch, "E222", {"start": v(-37.89, -44.59) * mm, "end": v(-37.89, -13.62) * mm});
            skLineSegment(sketch, "E223", {"start": v(-37.89, -13.62) * mm, "end": v(-44.39, -9.98) * mm});
            skArc(sketch, "E224", {"start": v(-44.39, -9.98) * mm, "mid": v(-46.48, -8.8) * mm, "end": v(-48.54, -7.56) * mm});
            skArc(sketch, "E225", {"start": v(-48.54, -7.56) * mm, "mid": v(-49.35, -6.98) * mm, "end": v(-50.05, -6.26) * mm});
            skArc(sketch, "E226", {"start": v(-50.05, -6.26) * mm, "mid": v(-50.48, -5.56) * mm, "end": v(-50.7, -4.76) * mm});
            skArc(sketch, "E227", {"start": v(-50.7, -4.76) * mm, "mid": v(-50.84, -3.4) * mm, "end": v(-50.89, -2.05) * mm});
            skLineSegment(sketch, "E228", {"start": v(-50.89, -2.05) * mm, "end": v(-50.89, 2.25) * mm});
            skLineSegment(sketch, "E229", {"start": v(-50.89, 2.25) * mm, "end": v(-60.88, 8.9) * mm});
            skArc(sketch, "E230", {"start": v(-60.88, 8.9) * mm, "mid": v(-62.81, 10.18) * mm, "end": v(-64.75, 11.45) * mm});
            skArc(sketch, "E231", {"start": v(-64.75, 11.45) * mm, "mid": v(-66.42, 12.53) * mm, "end": v(-68.1, 13.6) * mm});
            skArc(sketch, "E232", {"start": v(-68.1, 13.6) * mm, "mid": v(-69.56, 14.52) * mm, "end": v(-71.03, 15.44) * mm});
            skArc(sketch, "E233", {"start": v(-71.03, 15.44) * mm, "mid": v(-71.22, 15.53) * mm, "end": v(-71.42, 15.56) * mm});
            skArc(sketch, "E234", {"start": v(-71.42, 15.56) * mm, "mid": v(-71.56, 15.5) * mm, "end": v(-71.63, 15.35) * mm});
            skArc(sketch, "E235", {"start": v(-71.63, 15.35) * mm, "mid": v(-71.64, 14.4) * mm, "end": v(-71.64, 13.43) * mm});
            skArc(sketch, "E236", {"start": v(-71.64, 13.43) * mm, "mid": v(-71.63, 12.26) * mm, "end": v(-71.58, 11.09) * mm});
            skArc(sketch, "E237", {"start": v(-71.58, 11.09) * mm, "mid": v(-71.5, 9.7) * mm, "end": v(-71.4, 8.3) * mm});
            skArc(sketch, "E238", {"start": v(60.86, 8.85) * mm, "mid": v(57.67, 6.64) * mm, "end": v(54.49, 4.4) * mm});
            skArc(sketch, "E239", {"start": v(54.49, 4.4) * mm, "mid": v(53.36, 3.5) * mm, "end": v(52.34, 2.47) * mm});
            skArc(sketch, "E240", {"start": v(52.34, 2.47) * mm, "mid": v(51.76, 1.63) * mm, "end": v(51.41, 0.66) * mm});
            skArc(sketch, "E241", {"start": v(51.41, 0.66) * mm, "mid": v(51.19, -0.69) * mm, "end": v(51.11, -2.06) * mm});
            skArc(sketch, "E242", {"start": v(51.11, -2.06) * mm, "mid": v(51.06, -3.38) * mm, "end": v(50.92, -4.7) * mm});
            skArc(sketch, "E243", {"start": v(50.92, -4.7) * mm, "mid": v(50.7, -5.5) * mm, "end": v(50.26, -6.2) * mm});
            skArc(sketch, "E244", {"start": v(50.26, -6.2) * mm, "mid": v(49.56, -6.91) * mm, "end": v(48.75, -7.5) * mm});
            skArc(sketch, "E245", {"start": v(48.75, -7.5) * mm, "mid": v(46.69, -8.72) * mm, "end": v(44.61, -9.9) * mm});
            skLineSegment(sketch, "E246", {"start": v(44.61, -9.9) * mm, "end": v(38.11, -13.54) * mm});
            skLineSegment(sketch, "E247", {"start": v(38.11, -13.54) * mm, "end": v(38.11, -44.62) * mm});
            skArc(sketch, "E248", {"start": v(38.11, -44.62) * mm, "mid": v(38.12, -52.66) * mm, "end": v(38.16, -60.7) * mm});
            skArc(sketch, "E249", {"start": v(38.16, -60.7) * mm, "mid": v(38.23, -64.96) * mm, "end": v(38.36, -69.22) * mm});
            skArc(sketch, "E250", {"start": v(38.36, -69.22) * mm, "mid": v(38.5, -71.83) * mm, "end": v(38.68, -74.44) * mm});
            skArc(sketch, "E251", {"start": v(38.68, -74.44) * mm, "mid": v(38.93, -74.8) * mm, "end": v(39.36, -74.74) * mm});
            skArc(sketch, "E252", {"start": v(39.36, -74.74) * mm, "mid": v(43.95, -71.19) * mm, "end": v(48.47, -67.54) * mm});
            skArc(sketch, "E253", {"start": v(48.47, -67.54) * mm, "mid": v(53.34, -63.45) * mm, "end": v(58.15, -59.29) * mm});
            skArc(sketch, "E254", {"start": v(58.15, -59.29) * mm, "mid": v(62.78, -55.2) * mm, "end": v(67.39, -51.09) * mm});
            skArc(sketch, "E255", {"start": v(67.39, -51.09) * mm, "mid": v(67.92, -50.35) * mm, "end": v(68.11, -49.46) * mm});
            skArc(sketch, "E256", {"start": v(68.11, -49.46) * mm, "mid": v(68.14, -47.35) * mm, "end": v(68.24, -45.24) * mm});
            skArc(sketch, "E257", {"start": v(68.24, -45.24) * mm, "mid": v(68.94, -33.3) * mm, "end": v(69.65, -21.37) * mm});
            skArc(sketch, "E258", {"start": v(69.65, -21.37) * mm, "mid": v(70.33, -9.99) * mm, "end": v(71.03, 1.39) * mm});
            skArc(sketch, "E259", {"start": v(71.03, 1.39) * mm, "mid": v(71.3, 5.35) * mm, "end": v(71.62, 9.3) * mm});
            skArc(sketch, "E260", {"start": v(71.62, 9.3) * mm, "mid": v(71.7, 10.5) * mm, "end": v(71.77, 11.7) * mm});
            skArc(sketch, "E261", {"start": v(71.77, 11.7) * mm, "mid": v(71.8, 12.7) * mm, "end": v(71.78, 13.72) * mm});
            skArc(sketch, "E262", {"start": v(71.78, 13.72) * mm, "mid": v(71.74, 14.5) * mm, "end": v(71.68, 15.3) * mm});
            skArc(sketch, "E263", {"start": v(71.68, 15.3) * mm, "mid": v(71.58, 15.48) * mm, "end": v(71.4, 15.55) * mm});
            skArc(sketch, "E264", {"start": v(71.4, 15.55) * mm, "mid": v(71.11, 15.5) * mm, "end": v(70.85, 15.4) * mm});
            skArc(sketch, "E265", {"start": v(70.85, 15.4) * mm, "mid": v(69.41, 14.49) * mm, "end": v(67.98, 13.58) * mm});
            skArc(sketch, "E266", {"start": v(67.98, 13.58) * mm, "mid": v(66.31, 12.5) * mm, "end": v(64.66, 11.42) * mm});
            skArc(sketch, "E267", {"start": v(64.66, 11.42) * mm, "mid": v(62.75, 10.14) * mm, "end": v(60.86, 8.85) * mm});
            skLineSegment(sketch, "E268", {"start": v(-25.64, -10.42) * mm, "end": v(-35.89, -15.3) * mm});
            skLineSegment(sketch, "E269", {"start": v(-35.89, -15.3) * mm, "end": v(-35.89, -46.24) * mm});
            skLineSegment(sketch, "E270", {"start": v(-35.89, -46.24) * mm, "end": v(-35.89, -77.17) * mm});
            skLineSegment(sketch, "E271", {"start": v(-35.89, -77.17) * mm, "end": v(-30.93, -81.8) * mm});
            skArc(sketch, "E272", {"start": v(-30.93, -81.8) * mm, "mid": v(-29.96, -82.7) * mm, "end": v(-28.97, -83.58) * mm});
            skArc(sketch, "E273", {"start": v(-28.97, -83.58) * mm, "mid": v(-28.1, -84.34) * mm, "end": v(-27.2, -85.08) * mm});
            skArc(sketch, "E274", {"start": v(-27.2, -85.08) * mm, "mid": v(-26.44, -85.68) * mm, "end": v(-25.67, -86.28) * mm});
            skArc(sketch, "E275", {"start": v(-25.67, -86.28) * mm, "mid": v(-25.44, -86.4) * mm, "end": v(-25.18, -86.44) * mm});
            skArc(sketch, "E276", {"start": v(-25.18, -86.44) * mm, "mid": v(-24.92, -86.37) * mm, "end": v(-24.75, -86.17) * mm});
            skArc(sketch, "E277", {"start": v(-24.75, -86.17) * mm, "mid": v(-23.97, -84.47) * mm, "end": v(-23.2, -82.77) * mm});
            skArc(sketch, "E278", {"start": v(-23.2, -82.77) * mm, "mid": v(-22.32, -80.76) * mm, "end": v(-21.47, -78.74) * mm});
            skArc(sketch, "E279", {"start": v(-21.47, -78.74) * mm, "mid": v(-20.5, -76.35) * mm, "end": v(-19.57, -73.94) * mm});
            skLineSegment(sketch, "E280", {"start": v(-19.57, -73.94) * mm, "end": v(-14.75, -61.44) * mm});
            skLineSegment(sketch, "E281", {"start": v(-14.75, -61.44) * mm, "end": v(0.05, -61.44) * mm});
            skLineSegment(sketch, "E282", {"start": v(0.05, -61.44) * mm, "end": v(14.85, -61.44) * mm});
            skLineSegment(sketch, "E283", {"start": v(14.85, -61.44) * mm, "end": v(19.67, -73.94) * mm});
            skArc(sketch, "E284", {"start": v(19.67, -73.94) * mm, "mid": v(20.61, -76.34) * mm, "end": v(21.57, -78.74) * mm});
            skArc(sketch, "E285", {"start": v(21.57, -78.74) * mm, "mid": v(22.41, -80.76) * mm, "end": v(23.28, -82.77) * mm});
            skArc(sketch, "E286", {"start": v(23.28, -82.77) * mm, "mid": v(24.05, -84.49) * mm, "end": v(24.82, -86.2) * mm});
            skArc(sketch, "E287", {"start": v(24.82, -86.2) * mm, "mid": v(24.97, -86.38) * mm, "end": v(25.2, -86.44) * mm});
            skArc(sketch, "E288", {"start": v(25.2, -86.44) * mm, "mid": v(25.43, -86.4) * mm, "end": v(25.64, -86.3) * mm});
            skArc(sketch, "E289", {"start": v(25.64, -86.3) * mm, "mid": v(26.42, -85.7) * mm, "end": v(27.2, -85.1) * mm});
            skArc(sketch, "E290", {"start": v(27.2, -85.1) * mm, "mid": v(28.1, -84.36) * mm, "end": v(29, -83.61) * mm});
            skArc(sketch, "E291", {"start": v(29, -83.61) * mm, "mid": v(30, -82.74) * mm, "end": v(31, -81.85) * mm});
            skLineSegment(sketch, "E292", {"start": v(31, -81.85) * mm, "end": v(36.11, -77.26) * mm});
            skLineSegment(sketch, "E293", {"start": v(36.11, -77.26) * mm, "end": v(36.11, -46.29) * mm});
            skLineSegment(sketch, "E294", {"start": v(36.11, -46.29) * mm, "end": v(36.11, -15.31) * mm});
            skLineSegment(sketch, "E295", {"start": v(36.11, -15.31) * mm, "end": v(25.57, -10.38) * mm});
            skArc(sketch, "E296", {"start": v(25.57, -10.38) * mm, "mid": v(23.54, -9.43) * mm, "end": v(21.5, -8.49) * mm});
            skArc(sketch, "E297", {"start": v(21.5, -8.49) * mm, "mid": v(19.75, -7.69) * mm, "end": v(18, -6.9) * mm});
            skArc(sketch, "E298", {"start": v(18, -6.9) * mm, "mid": v(16.45, -6.2) * mm, "end": v(14.91, -5.52) * mm});
            skArc(sketch, "E299", {"start": v(14.91, -5.52) * mm, "mid": v(14.75, -5.46) * mm, "end": v(14.57, -5.44) * mm});
            skArc(sketch, "E300", {"start": v(14.57, -5.44) * mm, "mid": v(14.44, -5.5) * mm, "end": v(14.38, -5.63) * mm});
            skArc(sketch, "E301", {"start": v(14.38, -5.63) * mm, "mid": v(14.31, -8.62) * mm, "end": v(14.25, -11.61) * mm});
            skArc(sketch, "E302", {"start": v(14.25, -11.61) * mm, "mid": v(14.18, -15) * mm, "end": v(14.15, -18.4) * mm});
            skArc(sketch, "E303", {"start": v(14.15, -18.4) * mm, "mid": v(14.12, -22.42) * mm, "end": v(14.11, -26.44) * mm});
            skLineSegment(sketch, "E304", {"start": v(14.11, -26.44) * mm, "end": v(14.11, -47.44) * mm});
            skLineSegment(sketch, "E305", {"start": v(14.11, -47.44) * mm, "end": v(0.11, -47.44) * mm});
            skLineSegment(sketch, "E306", {"start": v(0.11, -47.44) * mm, "end": v(-13.89, -47.44) * mm});
            skLineSegment(sketch, "E307", {"start": v(-13.89, -47.44) * mm, "end": v(-13.89, -26.44) * mm});
            skArc(sketch, "E308", {"start": v(-13.89, -26.44) * mm, "mid": v(-13.9, -22.42) * mm, "end": v(-13.94, -18.4) * mm});
            skArc(sketch, "E309", {"start": v(-13.94, -18.4) * mm, "mid": v(-14, -15) * mm, "end": v(-14.1, -11.63) * mm});
            skArc(sketch, "E310", {"start": v(-14.1, -11.63) * mm, "mid": v(-14.22, -8.7) * mm, "end": v(-14.33, -5.76) * mm});
            skArc(sketch, "E311", {"start": v(-14.33, -5.76) * mm, "mid": v(-14.43, -5.56) * mm, "end": v(-14.64, -5.49) * mm});
            skArc(sketch, "E312", {"start": v(-14.64, -5.49) * mm, "mid": v(-14.91, -5.53) * mm, "end": v(-15.18, -5.62) * mm});
            skArc(sketch, "E313", {"start": v(-15.18, -5.62) * mm, "mid": v(-16.68, -6.28) * mm, "end": v(-18.18, -6.95) * mm});
            skArc(sketch, "E314", {"start": v(-18.18, -6.95) * mm, "mid": v(-19.92, -7.74) * mm, "end": v(-21.66, -8.54) * mm});
            skArc(sketch, "E315", {"start": v(-21.66, -8.54) * mm, "mid": v(-23.65, -9.47) * mm, "end": v(-25.64, -10.42) * mm});
            skArc(sketch, "E316", {"start": v(-18.19, -76.13) * mm, "mid": v(-19.08, -78.38) * mm, "end": v(-19.95, -80.64) * mm});
            skArc(sketch, "E317", {"start": v(-19.95, -80.64) * mm, "mid": v(-20.68, -82.56) * mm, "end": v(-21.38, -84.48) * mm});
            skArc(sketch, "E318", {"start": v(-21.38, -84.48) * mm, "mid": v(-21.98, -86.16) * mm, "end": v(-22.58, -87.85) * mm});
            skArc(sketch, "E319", {"start": v(-22.58, -87.85) * mm, "mid": v(-22.6, -88) * mm, "end": v(-22.52, -88.15) * mm});
            skArc(sketch, "E320", {"start": v(-22.52, -88.15) * mm, "mid": v(-22.37, -88.25) * mm, "end": v(-22.2, -88.28) * mm});
            skArc(sketch, "E321", {"start": v(-22.2, -88.28) * mm, "mid": v(-18.93, -88.3) * mm, "end": v(-15.66, -88.3) * mm});
            skArc(sketch, "E322", {"start": v(-15.66, -88.3) * mm, "mid": v(-12, -88.3) * mm, "end": v(-8.32, -88.3) * mm});
            skArc(sketch, "E323", {"start": v(-8.32, -88.3) * mm, "mid": v(-3.99, -88.26) * mm, "end": v(0.34, -88.21) * mm});
            skLineSegment(sketch, "E324", {"start": v(0.34, -88.21) * mm, "end": v(22.86, -87.94) * mm});
            skLineSegment(sketch, "E325", {"start": v(22.86, -87.94) * mm, "end": v(18.35, -76.2) * mm});
            skLineSegment(sketch, "E326", {"start": v(18.35, -76.2) * mm, "end": v(13.84, -64.44) * mm});
            skLineSegment(sketch, "E327", {"start": v(13.84, -64.44) * mm, "end": v(0.16, -64.44) * mm});
            skLineSegment(sketch, "E328", {"start": v(0.16, -64.44) * mm, "end": v(-13.53, -64.44) * mm});
            skLineSegment(sketch, "E329", {"start": v(-13.53, -64.44) * mm, "end": v(-18.19, -76.13) * mm});
            skSolve(sketch);
        }
        {
            var Q0;
            Q0=makeQuery(id+"F0.imprint","IMPRINT",FACE,{"disambiguationData":[TD([[makeQuery(id+"F0.imprint","IMPRINT",EDGE,{"derivedFrom":sQuery(id+"F0.wireOp",EDGE,"E268")}),1.0]])]});
            var Q1;
            Q1=makeQuery(id+"F0.imprint","IMPRINT",FACE,{"disambiguationData":[TD([[makeQuery(id+"F0.imprint","IMPRINT",EDGE,{"derivedFrom":sQuery(id+"F0.wireOp",EDGE,"E180")}),1.0]])]});
            var Q2;
            Q2=makeQuery(id+"F0.imprint","IMPRINT",FACE,{"disambiguationData":[TD([[makeQuery(id+"F0.imprint","IMPRINT",EDGE,{"derivedFrom":sQuery(id+"F0.wireOp",EDGE,"E210")}),1.0]])]});
            var Q3;
            Q3=makeQuery(id+"F0.imprint","IMPRINT",FACE,{"disambiguationData":[TD([[makeQuery(id+"F0.imprint","IMPRINT",EDGE,{"derivedFrom":sQuery(id+"F0.wireOp",EDGE,"E316")}),1.0]])]});
            var Q4;
            Q4=makeQuery(id+"F0.imprint","IMPRINT",FACE,{"disambiguationData":[TD([[makeQuery(id+"F0.imprint","IMPRINT",EDGE,{"derivedFrom":sQuery(id+"F0.wireOp",EDGE,"E238")}),1.0]])]});
            var Q5;
            Q5=makeQuery(id+"F0.imprint","IMPRINT",FACE,{"disambiguationData":[TD([[makeQuery(id+"F0.imprint","IMPRINT",EDGE,{"derivedFrom":sQuery(id+"F0.wireOp",EDGE,"E108")}),1.0]])]});
            var Q6;
            Q6=makeQuery(id+"F0.imprint","IMPRINT",FACE,{"disambiguationData":[TD([[makeQuery(id+"F0.imprint","IMPRINT",EDGE,{"derivedFrom":sQuery(id+"F0.wireOp",EDGE,"E0")}),1.0]])]});
            var Q7;
            Q7=makeQuery(id+"F0.imprint","IMPRINT",FACE,{"disambiguationData":[TD([[makeQuery(id+"F0.imprint","IMPRINT",EDGE,{"derivedFrom":sQuery(id+"F0.wireOp",EDGE,"E48")}),1.0]])]});
            extrude(context, id + "F1", {"entities" : qUnion([Q0, Q1, Q2, Q3, Q4, Q5, Q6, Q7]), "depth" : 25 * mm, "offsetDistance" : 25 * mm});
        }
    });
